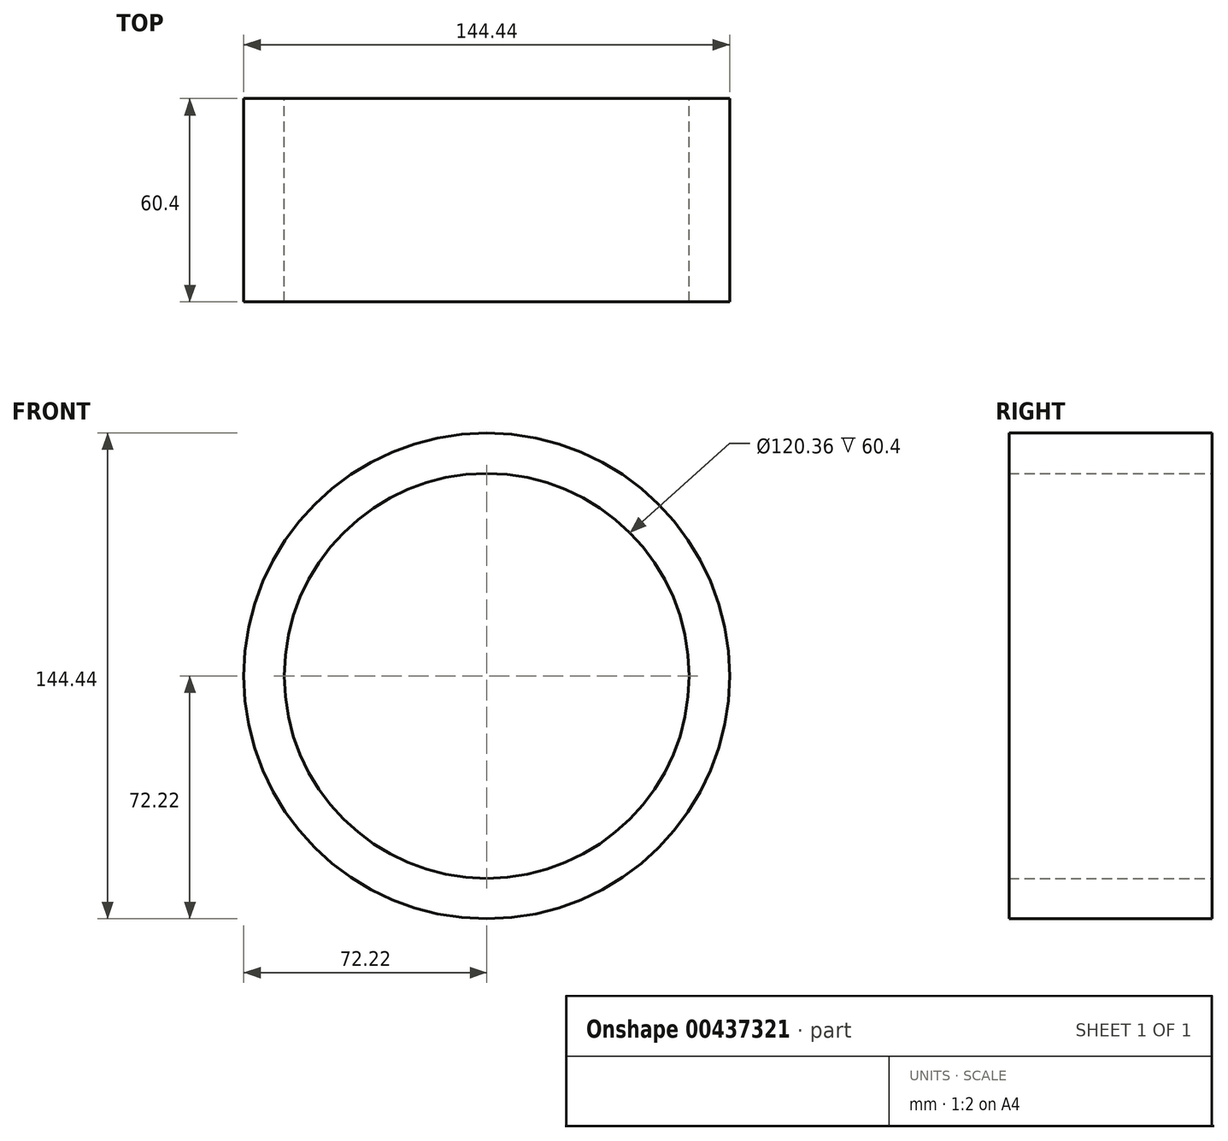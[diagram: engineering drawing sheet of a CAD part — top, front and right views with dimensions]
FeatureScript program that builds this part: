
annotation { "Feature Type Name" : "Feature", "Feature Type Description" : "" }
export const myFeature = defineFeature(function(context is Context, id is Id, definition is map)
    precondition{}
    {
        {
            var Q0;
            Q0=qCreatedBy(makeId("Front.planeOp"),FACE);
            var sketch = newSketch(context, id + "F0", { "sketchPlane" : qUnion([Q0])});
            skCircle(sketch, "E0", {"center": v(0, 0) * mm, "radius": 72.22 * mm});
            skSolve(sketch);
        }
        {
            var Q0;
            Q0 = qSketchRegion(id + "F0", true);
            extrude(context, id + "F1", {"entities" : qUnion([Q0]), "depth" : 10 * mm});
        }
        {
            var Q0;
            Q0=makeQuery(id+"F1.opExtrude","CAP_FACE",FACE,{"disambiguationData":[OSD([sQuery(id+"F0.wireOp",EDGE,"E0")])],"isStart":false});
            var sketch = newSketch(context, id + "F2", { "sketchPlane" : qUnion([Q0])});
            skSolve(sketch);
        }
        {
            var Q0;
            Q0=makeQuery(id+"F2.imprint","IMPRINT",FACE,{"disambiguationData":[TD([[makeQuery(id+"F2.imprint","IMPRINT",EDGE,{"derivedFrom":makeQuery(id+"F1.opExtrude","CAP_EDGE",EDGE,{"disambiguationData":[OSD([sQuery(id+"F0.wireOp",EDGE,"E0")])],"isStart":false})}),1.0]])]});
            extrude(context, id + "F3", {"entities" : qUnion([Q0]), "operationType" : NewBodyOperationType.ADD, "depth" : 25.4 * mm});
        }
        {
            var Q0;
            Q0=makeQuery(id+"F1.opExtrude","CAP_FACE",FACE,{"disambiguationData":[OSD([sQuery(id+"F0.wireOp",EDGE,"E0")])],"isStart":true});
            var sketch = newSketch(context, id + "F4", { "sketchPlane" : qUnion([Q0])});
            skCircle(sketch, "E1", {"center": v(0, 0) * mm, "radius": 60.18 * mm});
            skSolve(sketch);
        }
        {
            var Q0;
            Q0=qCreatedBy(makeId("Front.planeOp"),FACE);
            var sketch = newSketch(context, id + "F5", { "sketchPlane" : qUnion([Q0])});
            skCircle(sketch, "E2", {"center": v(0, 13.37) * mm, "radius": 13.37 * mm});
            skSolve(sketch);
        }
        {
            var Q0;
            Q0 = qSketchRegion(id + "F5", true);
            extrude(context, id + "F6", {"entities" : qUnion([Q0]), "operationType" : NewBodyOperationType.REMOVE, "endBound" : BoundingType.THROUGH_ALL, "oppositeDirection" : true, "depth" : 25 * mm});
        }
        {
            var Q0;
            Q0=makeQuery(id+"F4.imprint","IMPRINT",FACE,{"disambiguationData":[TD([[makeQuery(id+"F4.imprint","IMPRINT",EDGE,{"derivedFrom":sQuery(id+"F4.wireOp",EDGE,"E1")}),1.0]])]});
            extrude(context, id + "F7", {"entities" : qUnion([Q0]), "operationType" : NewBodyOperationType.REMOVE, "oppositeDirection" : true, "depth" : 139.58 * mm});
        }
        {
            var Q0;
            Q0=makeQuery(id+"F3.opExtrude","CAP_FACE",FACE,{"disambiguationData":[OSD([sQuery(id+"F0.wireOp",EDGE,"E0")])],"isStart":false});
            extrude(context, id + "F8", {"entities" : qUnion([Q0]), "operationType" : NewBodyOperationType.ADD, "depth" : 25 * mm});
        }
        {
            var Q0;
            Q0=qCreatedBy(makeId("Front.planeOp"),FACE);
            cPlane(context, id + "F9", {"entities" : qUnion([Q0]), "cplaneType" : CPlaneType.OFFSET, "offset" : 25 * mm, "width" : 150 * mm, "height" : 150 * mm});
        }
    });
